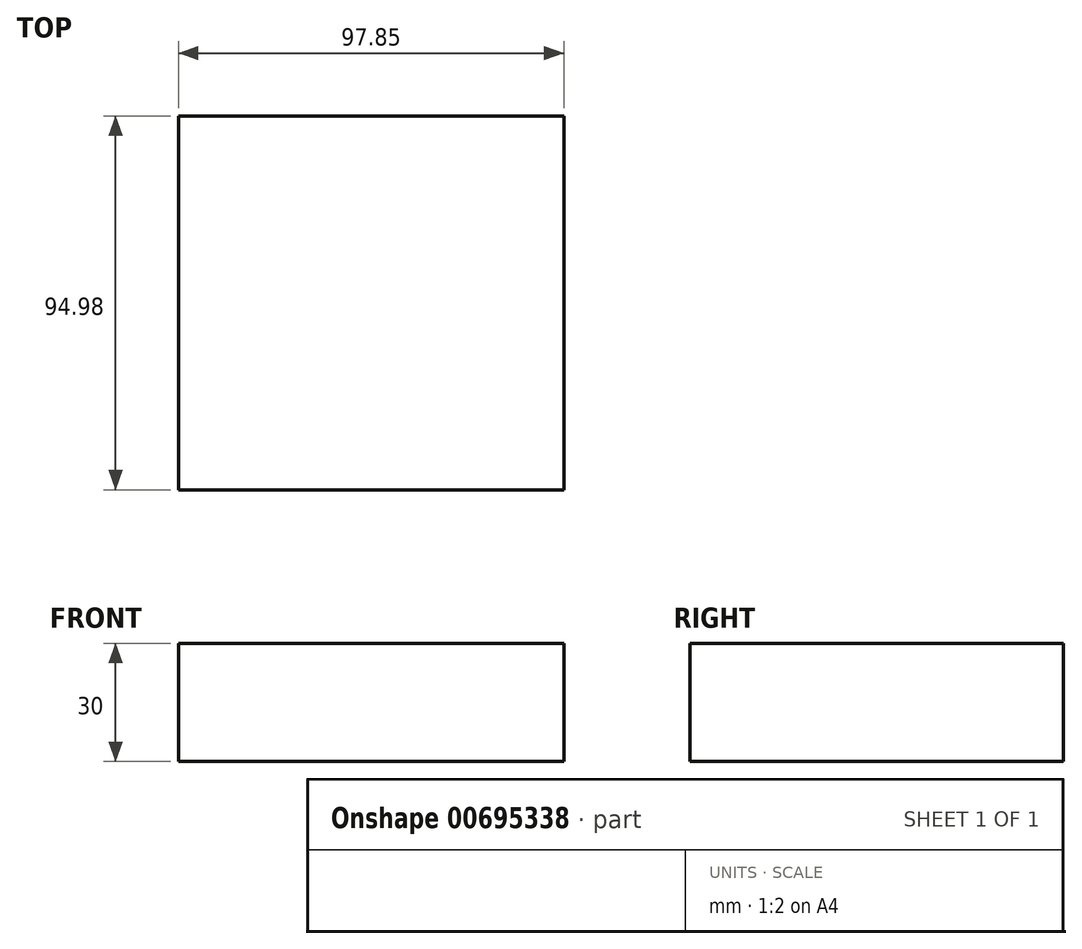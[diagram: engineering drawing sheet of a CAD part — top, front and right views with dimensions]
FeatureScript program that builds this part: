
annotation { "Feature Type Name" : "Feature", "Feature Type Description" : "" }
export const myFeature = defineFeature(function(context is Context, id is Id, definition is map)
    precondition{}
    {
        {
            var Q0;
            Q0=qCreatedBy(makeId("Top.planeOp"),FACE);
            var sketch = newSketch(context, id + "F0", { "sketchPlane" : qUnion([Q0])});
            skLineSegment(sketch, "E0.bottom", {"start": v(-47.63, 51.09) * mm, "end": v(50.22, 51.09) * mm});
            skLineSegment(sketch, "E0.top", {"start": v(-47.63, -43.9) * mm, "end": v(50.22, -43.9) * mm});
            skLineSegment(sketch, "E0.left", {"start": v(-47.63, 51.09) * mm, "end": v(-47.63, -43.9) * mm});
            skLineSegment(sketch, "E0.right", {"start": v(50.22, 51.09) * mm, "end": v(50.22, -43.9) * mm});
            skSolve(sketch);
        }
        {
            var Q0;
            Q0=makeQuery(id+"F0.imprint","IMPRINT",FACE,{"disambiguationData":[TD([[makeQuery(id+"F0.imprint","IMPRINT",EDGE,{"derivedFrom":sQuery(id+"F0.wireOp",EDGE,"E0.bottom")}),-1.0]])]});
            extrude(context, id + "F1", {"entities" : qUnion([Q0]), "depth" : 30 * mm, "offsetDistance" : 25.4 * mm});
        }
        {
            var Q0;
            Q0=makeQuery(id+"F1.opExtrude","CAP_FACE",FACE,{"disambiguationData":[OSD([sQuery(id+"F0.wireOp",EDGE,"E0.bottom"),sQuery(id+"F0.wireOp",EDGE,"E0.top"),sQuery(id+"F0.wireOp",EDGE,"E0.left"),sQuery(id+"F0.wireOp",EDGE,"E0.right")])],"isStart":false});
            var sketch = newSketch(context, id + "F2", { "sketchPlane" : qUnion([Q0])});
            skCircle(sketch, "E1", {"center": v(1.8, 0) * mm, "radius": 25.4 * mm});
            skSolve(sketch);
        }
        {
            var Q0;
            Q0=sQuery(id+"F2.wireOp",EDGE,"E1");
            extrude(context, id + "F3", {"bodyType" : ToolBodyType.SURFACE, "surfaceEntities" : qUnion([Q0]), "depth" : -20 * mm, "offsetDistance" : 25 * mm});
        }
    });
